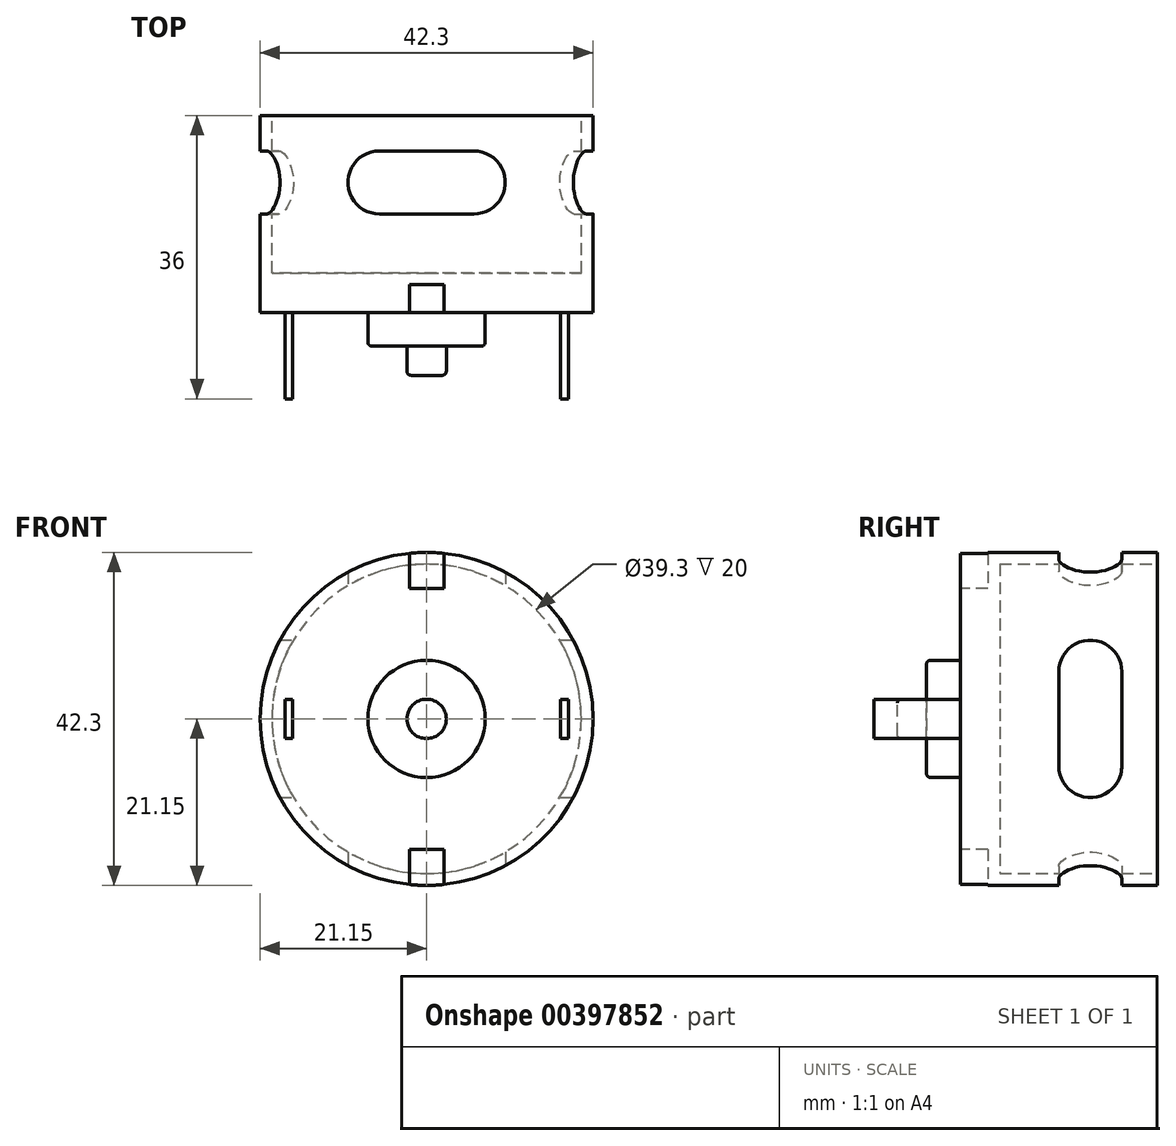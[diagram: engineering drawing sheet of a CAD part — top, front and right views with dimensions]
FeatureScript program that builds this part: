
annotation { "Feature Type Name" : "Feature", "Feature Type Description" : "" }
export const myFeature = defineFeature(function(context is Context, id is Id, definition is map)
    precondition{}
    {
        {
            var Q0;
            Q0=qCreatedBy(makeId("Front.planeOp"),FACE);
            var sketch = newSketch(context, id + "F0", { "sketchPlane" : qUnion([Q0])});
            skCircle(sketch, "E0", {"center": v(0, 0) * mm, "radius": 21.15 * mm});
            skPoint(sketch, "E1", {"position": v(-21.15, 0) * mm});
            skPoint(sketch, "E2", {"position": v(21.15, 0) * mm});
            skLineSegment(sketch, "E3", {"start": v(-21.15, 0) * mm, "end": v(21.15, 0) * mm, "construction": true});
            skPoint(sketch, "E4", {"position": v(-17.5, 0) * mm});
            skPoint(sketch, "E5", {"position": v(17.5, 0) * mm});
            skLineSegment(sketch, "E6.bottom", {"start": v(-17, 2.5) * mm, "end": v(-18, 2.5) * mm});
            skLineSegment(sketch, "E6.top", {"start": v(-17, -2.5) * mm, "end": v(-18, -2.5) * mm});
            skLineSegment(sketch, "E6.left", {"start": v(-17, 2.5) * mm, "end": v(-17, -2.5) * mm});
            skLineSegment(sketch, "E6.right", {"start": v(-18, 2.5) * mm, "end": v(-18, -2.5) * mm});
            skLineSegment(sketch, "E7.bottom", {"start": v(17, 2.5) * mm, "end": v(18, 2.5) * mm});
            skLineSegment(sketch, "E7.top", {"start": v(17, -2.5) * mm, "end": v(18, -2.5) * mm});
            skLineSegment(sketch, "E7.left", {"start": v(17, 2.5) * mm, "end": v(17, -2.5) * mm});
            skLineSegment(sketch, "E7.right", {"start": v(18, 2.5) * mm, "end": v(18, -2.5) * mm});
            skSolve(sketch);
        }
        {
            var Q0;
            Q0=makeQuery(id+"F0.imprint","IMPRINT",FACE,{"disambiguationData":[TD([[makeQuery(id+"F0.imprint","IMPRINT",EDGE,{"derivedFrom":sQuery(id+"F0.wireOp",EDGE,"E7.bottom")}),-1.0]])]});
            var Q1;
            Q1=makeQuery(id+"F0.imprint","IMPRINT",FACE,{"disambiguationData":[TD([[makeQuery(id+"F0.imprint","IMPRINT",EDGE,{"derivedFrom":sQuery(id+"F0.wireOp",EDGE,"E6.bottom")}),1.0]])]});
            extrude(context, id + "F1", {"entities" : qUnion([Q0, Q1]), "depth" : 11 * mm});
        }
        {
            var Q0;
            Q0 = qSketchRegion(id + "F0", true);
            var Q1;
            Q1=makeQuery(id+"F0.imprint","IMPRINT",FACE,{"disambiguationData":[TD([[makeQuery(id+"F0.imprint","IMPRINT",EDGE,{"derivedFrom":sQuery(id+"F0.wireOp",EDGE,"E6.bottom")}),1.0]])]});
            var Q2;
            Q2=makeQuery(id+"F0.imprint","IMPRINT",FACE,{"disambiguationData":[TD([[makeQuery(id+"F0.imprint","IMPRINT",EDGE,{"derivedFrom":sQuery(id+"F0.wireOp",EDGE,"E7.bottom")}),-1.0]])]});
            extrude(context, id + "F2", {"entities" : qUnion([Q0, Q1, Q2]), "oppositeDirection" : true, "depth" : 25 * mm});
        }
        {
            var Q0;
            Q0=makeQuery(id+"F2.opExtrude","CAP_FACE",FACE,{"disambiguationData":[OSD([sQuery(id+"F0.wireOp",EDGE,"E0"),sQuery(id+"F0.wireOp",EDGE,"E6.bottom"),sQuery(id+"F0.wireOp",EDGE,"E6.top"),sQuery(id+"F0.wireOp",EDGE,"E6.left"),sQuery(id+"F0.wireOp",EDGE,"E6.right"),sQuery(id+"F0.wireOp",EDGE,"E7.bottom"),sQuery(id+"F0.wireOp",EDGE,"E7.top"),sQuery(id+"F0.wireOp",EDGE,"E7.left"),sQuery(id+"F0.wireOp",EDGE,"E7.right")])],"isStart":false});
            var sketch = newSketch(context, id + "F3", { "sketchPlane" : qUnion([Q0])});
            skCircle(sketch, "E8", {"center": v(0, 0) * mm, "radius": 19.65 * mm});
            skSolve(sketch);
        }
        {
            var Q0;
            Q0 = qSketchRegion(id + "F3", true);
            extrude(context, id + "F4", {"entities" : qUnion([Q0]), "operationType" : NewBodyOperationType.REMOVE, "oppositeDirection" : true, "depth" : 20 * mm});
        }
        {
            var Q0;
            Q0=qCreatedBy(makeId("Right.planeOp"),FACE);
            var sketch = newSketch(context, id + "F5", { "sketchPlane" : qUnion([Q0])});
            skPoint(sketch, "E9", {"position": v(16.5, 0) * mm});
            skLineSegment(sketch, "E10.bottom", {"start": v(20.5, 10) * mm, "end": v(12.5, 10) * mm});
            skLineSegment(sketch, "E10.top", {"start": v(20.5, -10) * mm, "end": v(12.5, -10) * mm});
            skLineSegment(sketch, "E10.left", {"start": v(20.5, 10) * mm, "end": v(20.5, -10) * mm});
            skLineSegment(sketch, "E10.right", {"start": v(12.5, 10) * mm, "end": v(12.5, -10) * mm});
            skPoint(sketch, "E11", {"position": v(16.5, 6) * mm});
            skPoint(sketch, "E12", {"position": v(16.5, -6) * mm});
            skArc(sketch, "E13", {"start": v(12.5, 6) * mm, "mid": v(16.5, 10) * mm, "end": v(20.5, 6) * mm});
            skArc(sketch, "E14", {"start": v(20.5, -6) * mm, "mid": v(16.5, -10) * mm, "end": v(12.5, -6) * mm});
            skSolve(sketch);
        }
        {
            var Q0;
            {var subQ0=sQuery(id+"F5.wireOp",EDGE,"E13");var subQ1=sQuery(id+"F5.wireOp",EDGE,"E10.left");var subQ2=makeQuery(id+"F5.imprint","INTERSECT",VERTEX,{"derivedFrom":[subQ1,subQ0]});Q0=makeQuery(id+"F5.imprint","IMPRINT",FACE,{"disambiguationData":[TD([[makeQuery(id+"F5.imprint","IMPRINT",EDGE,{"disambiguationData":[TD([[subQ2,-1.0]])],"derivedFrom":subQ1}),-1.0]])]});}
            extrude(context, id + "F6", {"entities" : qUnion([Q0]), "operationType" : NewBodyOperationType.REMOVE, "endBound" : BoundingType.SYMMETRIC, "oppositeDirection" : true, "depth" : 45 * mm});
        }
        {
            var Q0;
            Q0=qCreatedBy(makeId("Top.planeOp"),FACE);
            var sketch = newSketch(context, id + "F7", { "sketchPlane" : qUnion([Q0])});
            skPoint(sketch, "E15", {"position": v(0, 16.5) * mm});
            skLineSegment(sketch, "E16.bottom", {"start": v(-10, 20.5) * mm, "end": v(10, 20.5) * mm});
            skLineSegment(sketch, "E16.top", {"start": v(-10, 12.5) * mm, "end": v(10, 12.5) * mm});
            skLineSegment(sketch, "E16.left", {"start": v(-10, 20.5) * mm, "end": v(-10, 12.5) * mm});
            skLineSegment(sketch, "E16.right", {"start": v(10, 20.5) * mm, "end": v(10, 12.5) * mm});
            skPoint(sketch, "E17", {"position": v(-6, 16.5) * mm});
            skPoint(sketch, "E18", {"position": v(6, 16.5) * mm});
            skArc(sketch, "E19", {"start": v(-6, 12.5) * mm, "mid": v(-10, 16.5) * mm, "end": v(-6, 20.5) * mm});
            skArc(sketch, "E20", {"start": v(6, 20.5) * mm, "mid": v(10, 16.5) * mm, "end": v(6, 12.5) * mm});
            skSolve(sketch);
        }
        {
            var Q0;
            {var subQ0=sQuery(id+"F7.wireOp",EDGE,"E19");var subQ6=sQuery(id+"F7.wireOp",EDGE,"E16.bottom");var subQ7=makeQuery(id+"F7.imprint","INTERSECT",VERTEX,{"derivedFrom":[subQ6,subQ0]});Q0=makeQuery(id+"F7.imprint","IMPRINT",FACE,{"disambiguationData":[TD([[makeQuery(id+"F7.imprint","IMPRINT",EDGE,{"disambiguationData":[TD([[subQ7,-1.0]])],"derivedFrom":subQ6}),-1.0]])]});}
            extrude(context, id + "F8", {"entities" : qUnion([Q0]), "operationType" : NewBodyOperationType.REMOVE, "endBound" : BoundingType.SYMMETRIC, "depth" : 45 * mm});
        }
        {
            var Q0;
            Q0=makeQuery(id+"F2.opExtrude","CAP_FACE",FACE,{"disambiguationData":[OSD([sQuery(id+"F0.wireOp",EDGE,"E0")])],"isStart":true});
            var sketch = newSketch(context, id + "F9", { "sketchPlane" : qUnion([Q0])});
            skCircle(sketch, "E21", {"center": v(0, 0) * mm, "radius": 21.15 * mm});
            skPoint(sketch, "E22", {"position": v(0, 21.15) * mm});
            skPoint(sketch, "E23", {"position": v(0, -21.15) * mm});
            skLineSegment(sketch, "E24.bottom", {"start": v(-2.2, 25.75) * mm, "end": v(2.2, 25.75) * mm});
            skLineSegment(sketch, "E24.top", {"start": v(-2.2, 16.55) * mm, "end": v(2.2, 16.55) * mm});
            skLineSegment(sketch, "E24.left", {"start": v(-2.2, 25.75) * mm, "end": v(-2.2, 16.55) * mm});
            skLineSegment(sketch, "E24.right", {"start": v(2.2, 25.75) * mm, "end": v(2.2, 16.55) * mm});
            skLineSegment(sketch, "E25.bottom", {"start": v(-2.2, -16.55) * mm, "end": v(2.2, -16.55) * mm});
            skLineSegment(sketch, "E25.top", {"start": v(-2.2, -25.75) * mm, "end": v(2.2, -25.75) * mm});
            skLineSegment(sketch, "E25.left", {"start": v(-2.2, -16.55) * mm, "end": v(-2.2, -25.75) * mm});
            skLineSegment(sketch, "E25.right", {"start": v(2.2, -16.55) * mm, "end": v(2.2, -25.75) * mm});
            skSolve(sketch);
        }
        {
            var Q0;
            {var subQ5=sQuery(id+"F9.wireOp",EDGE,"E24.top");Q0=makeQuery(id+"F9.imprint","IMPRINT",FACE,{"disambiguationData":[TD([[makeQuery(id+"F9.imprint","IMPRINT",EDGE,{"derivedFrom":subQ5}),1.0]])]});}
            var Q1;
            {var subQ5=sQuery(id+"F9.wireOp",EDGE,"E25.bottom");Q1=makeQuery(id+"F9.imprint","IMPRINT",FACE,{"disambiguationData":[TD([[makeQuery(id+"F9.imprint","IMPRINT",EDGE,{"derivedFrom":subQ5}),-1.0]])]});}
            extrude(context, id + "F10", {"entities" : qUnion([Q0, Q1]), "operationType" : NewBodyOperationType.REMOVE, "oppositeDirection" : true, "depth" : 3.5 * mm});
        }
        {
            var Q0;
            Q0=makeQuery(id+"F2.opExtrude","CAP_FACE",FACE,{"disambiguationData":[OSD([sQuery(id+"F0.wireOp",EDGE,"E0")])],"isStart":true});
            var sketch = newSketch(context, id + "F11", { "sketchPlane" : qUnion([Q0])});
            skCircle(sketch, "E26", {"center": v(0, 0) * mm, "radius": 7.45 * mm});
            skCircle(sketch, "E27", {"center": v(0, 0) * mm, "radius": 2.5 * mm});
            skSolve(sketch);
        }
        {
            var Q0;
            Q0 = qSketchRegion(id + "F11", true);
            extrude(context, id + "F12", {"entities" : qUnion([Q0]), "operationType" : NewBodyOperationType.ADD, "depth" : 4.3 * mm});
        }
        {
            var Q0;
            Q0=makeQuery(id+"F12.boolean.opBoolean","SPLIT",FACE,{"disambiguationData":[TD([makeQuery(id+"F12.opExtrude","SWEPT_FACE",FACE,{"disambiguationData":[OSD([sQuery(id+"F11.wireOp",EDGE,"E27")])]})])],"derivedFrom":makeQuery(id+"F2.opExtrude","CAP_FACE",FACE,{"disambiguationData":[OSD([sQuery(id+"F0.wireOp",EDGE,"E0")])],"isStart":true})});
            extrude(context, id + "F13", {"entities" : qUnion([Q0]), "operationType" : NewBodyOperationType.ADD, "depth" : 8 * mm});
        }
        {
            var Q0;
            Q0=makeQuery(id+"F12.opExtrude","CAP_EDGE",EDGE,{"disambiguationData":[OSD([sQuery(id+"F11.wireOp",EDGE,"E26")])],"isStart":false});
            var Q1;
            Q1=makeQuery(id+"F13.opExtrude","CAP_EDGE",EDGE,{"disambiguationData":[OSD([sQuery(id+"F11.wireOp",EDGE,"E27")])],"isStart":false});
            fillet(context, id + "F14", {"entities" : qUnion([Q0, Q1]), "radius" : 0.5 * mm, "tangentPropagation" : true, "allowEdgeOverflow" : false});
        }
    });
